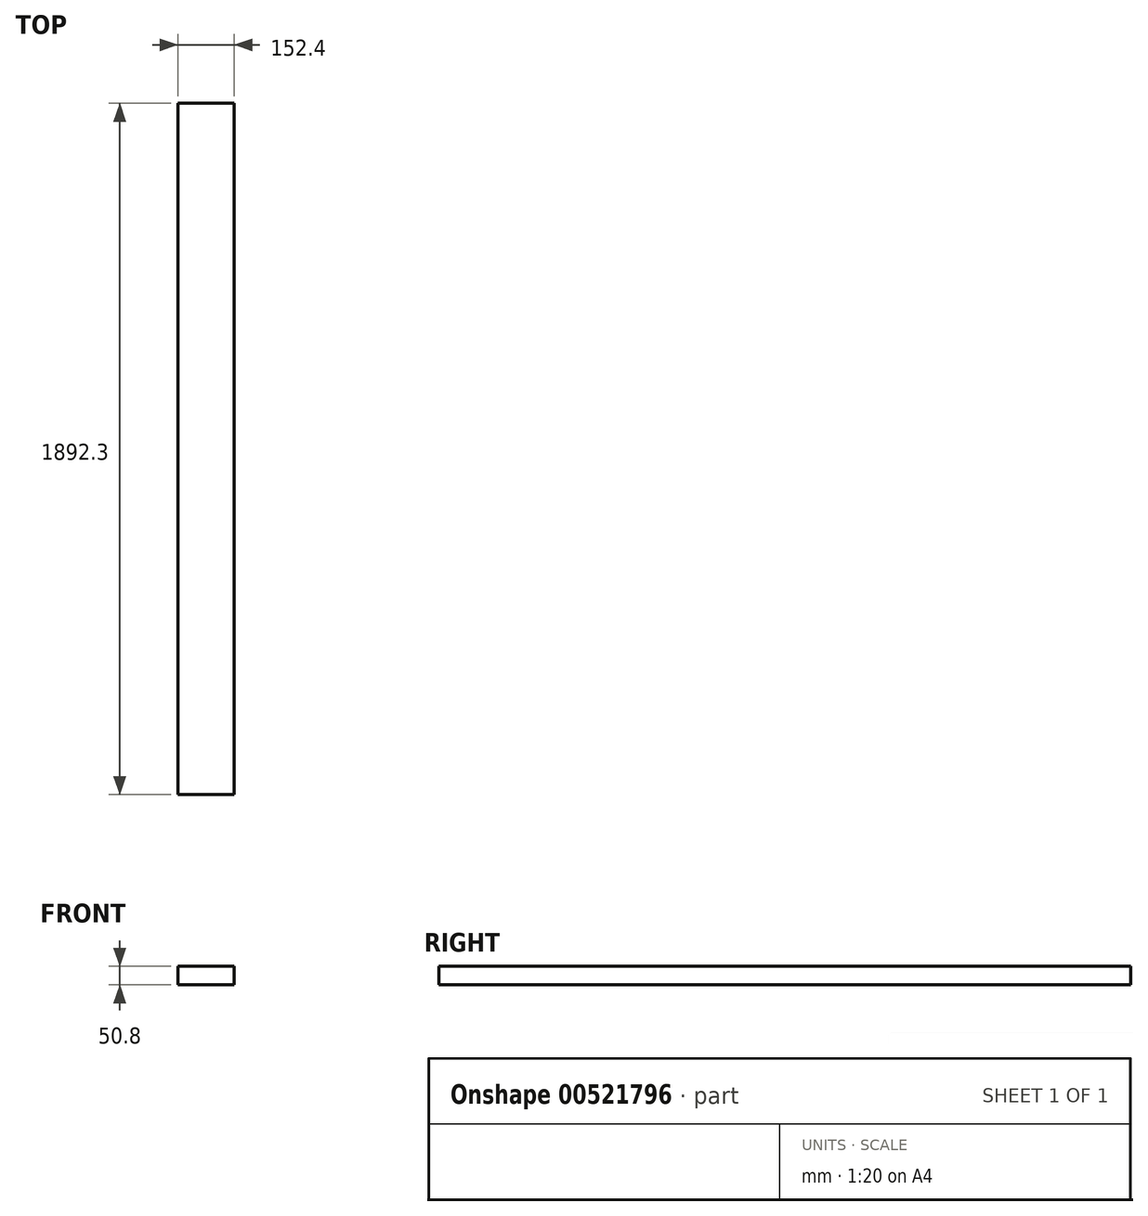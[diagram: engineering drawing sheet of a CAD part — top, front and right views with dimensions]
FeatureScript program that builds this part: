
annotation { "Feature Type Name" : "Feature", "Feature Type Description" : "" }
export const myFeature = defineFeature(function(context is Context, id is Id, definition is map)
    precondition{}
    {
        {
            var Q0;
            Q0=qCreatedBy(makeId("Front.planeOp"),FACE);
            var sketch = newSketch(context, id + "F0", { "sketchPlane" : qUnion([Q0])});
            skLineSegment(sketch, "E0.bottom", {"start": v(0, 0) * mm, "end": v(152.4, 0) * mm});
            skLineSegment(sketch, "E0.top", {"start": v(0, 50.8) * mm, "end": v(152.4, 50.8) * mm});
            skLineSegment(sketch, "E0.left", {"start": v(0, 0) * mm, "end": v(0, 50.8) * mm});
            skLineSegment(sketch, "E0.right", {"start": v(152.4, 0) * mm, "end": v(152.4, 50.8) * mm});
            skSolve(sketch);
        }
        {
            var Q0;
            Q0 = qSketchRegion(id + "F0", true);
            extrude(context, id + "F1", {"entities" : qUnion([Q0]), "oppositeDirection" : true, "depth" : 1892.3 * mm, "offsetDistance" : 25.4 * mm});
        }
    });
